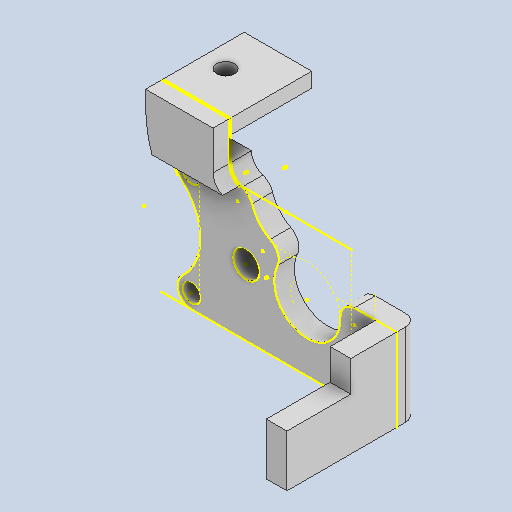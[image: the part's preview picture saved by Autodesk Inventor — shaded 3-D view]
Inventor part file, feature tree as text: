
AUTODESK INVENTOR PART (.ipt)
format: ipt  version: 2022 (Build 260153070, 153G)  size: 168,448 bytes
history: native  units: in
note: dims shown in document units (in); Inventor stores cm internally (conversion verified against a paired STEP export)
features: sketch x5, other x3
ambient origin geometry x8: Origin, YZ Plane, XZ Plane, XY Plane, X Axis, Y Axis, Z Axis, Center Point
bodies: Solid1 (feature_tree)
feature tree (8):
  other  "MotorEncoderBracket.ipt"
  other  "Solid1::MotorEncoderBracket.ipt"
  other  "TaggingFeature1"
  sketch  "Sketch1"  dims[d0=0.3937in]
  sketch  "Sketch2"
  sketch  "Sketch5"
  sketch  "Sketch6"
  sketch  "Sketch7"
